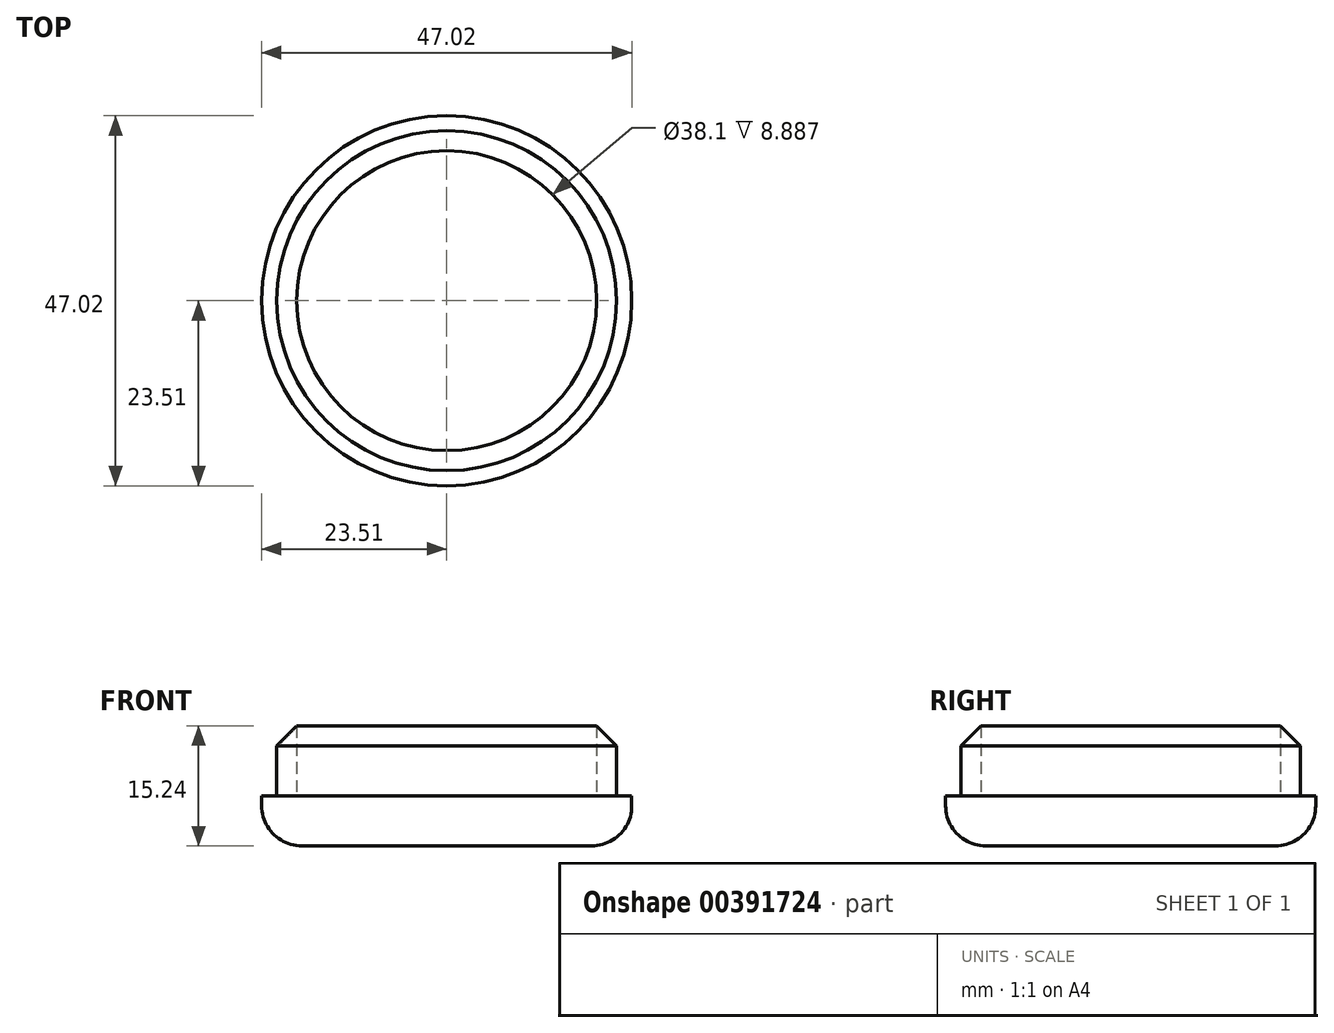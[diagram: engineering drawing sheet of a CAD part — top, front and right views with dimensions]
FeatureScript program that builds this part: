
annotation { "Feature Type Name" : "Feature", "Feature Type Description" : "" }
export const myFeature = defineFeature(function(context is Context, id is Id, definition is map)
    precondition{}
    {
        {
            var Q0;
            Q0=qCreatedBy(makeId("Top.planeOp"),FACE);
            var sketch = newSketch(context, id + "F0", { "sketchPlane" : qUnion([Q0])});
            skCircle(sketch, "E0", {"center": v(0, 0) * mm, "radius": 23.5 * mm});
            skSolve(sketch);
        }
        {
            var Q0;
            Q0=makeQuery(id+"F0.imprint","IMPRINT",FACE,{"disambiguationData":[TD([[makeQuery(id+"F0.imprint","IMPRINT",EDGE,{"derivedFrom":sQuery(id+"F0.wireOp",EDGE,"E0")}),1.0]])]});
            extrude(context, id + "F1", {"entities" : qUnion([Q0]), "depth" : 6.35 * mm});
        }
        {
            var Q0;
            Q0=qCreatedBy(makeId("Top.planeOp"),FACE);
            var sketch = newSketch(context, id + "F2", { "sketchPlane" : qUnion([Q0])});
            skCircle(sketch, "E1", {"center": v(0, 0) * mm, "radius": 21.59 * mm});
            skCircle(sketch, "E2", {"center": v(0, 0) * mm, "radius": 19.05 * mm});
            skSolve(sketch);
        }
        {
            var Q0;
            Q0=makeQuery(id+"F2.imprint","IMPRINT",FACE,{"disambiguationData":[TD([[makeQuery(id+"F2.imprint","IMPRINT",EDGE,{"derivedFrom":sQuery(id+"F2.wireOp",EDGE,"E1")}),1.0]])]});
            extrude(context, id + "F3", {"entities" : qUnion([Q0]), "operationType" : NewBodyOperationType.ADD, "depth" : 15.24 * mm});
        }
        {
            var Q0;
            Q0=makeQuery(id+"F1.opExtrude","CAP_EDGE",EDGE,{"disambiguationData":[OSD([sQuery(id+"F0.wireOp",EDGE,"E0")])],"isStart":true});
            fillet(context, id + "F4", {"entities" : qUnion([Q0]), "radius" : 5.08 * mm, "tangentPropagation" : true, "allowEdgeOverflow" : false});
        }
        {
            var Q0;
            Q0=makeQuery(id+"F3.opExtrude","CAP_EDGE",EDGE,{"disambiguationData":[OSD([sQuery(id+"F2.wireOp",EDGE,"E1")])],"isStart":false});
            chamfer(context, id + "F5", {"entities" : qUnion([Q0]), "width" : 2.54 * mm, "tangentPropagation" : true});
        }
    });
